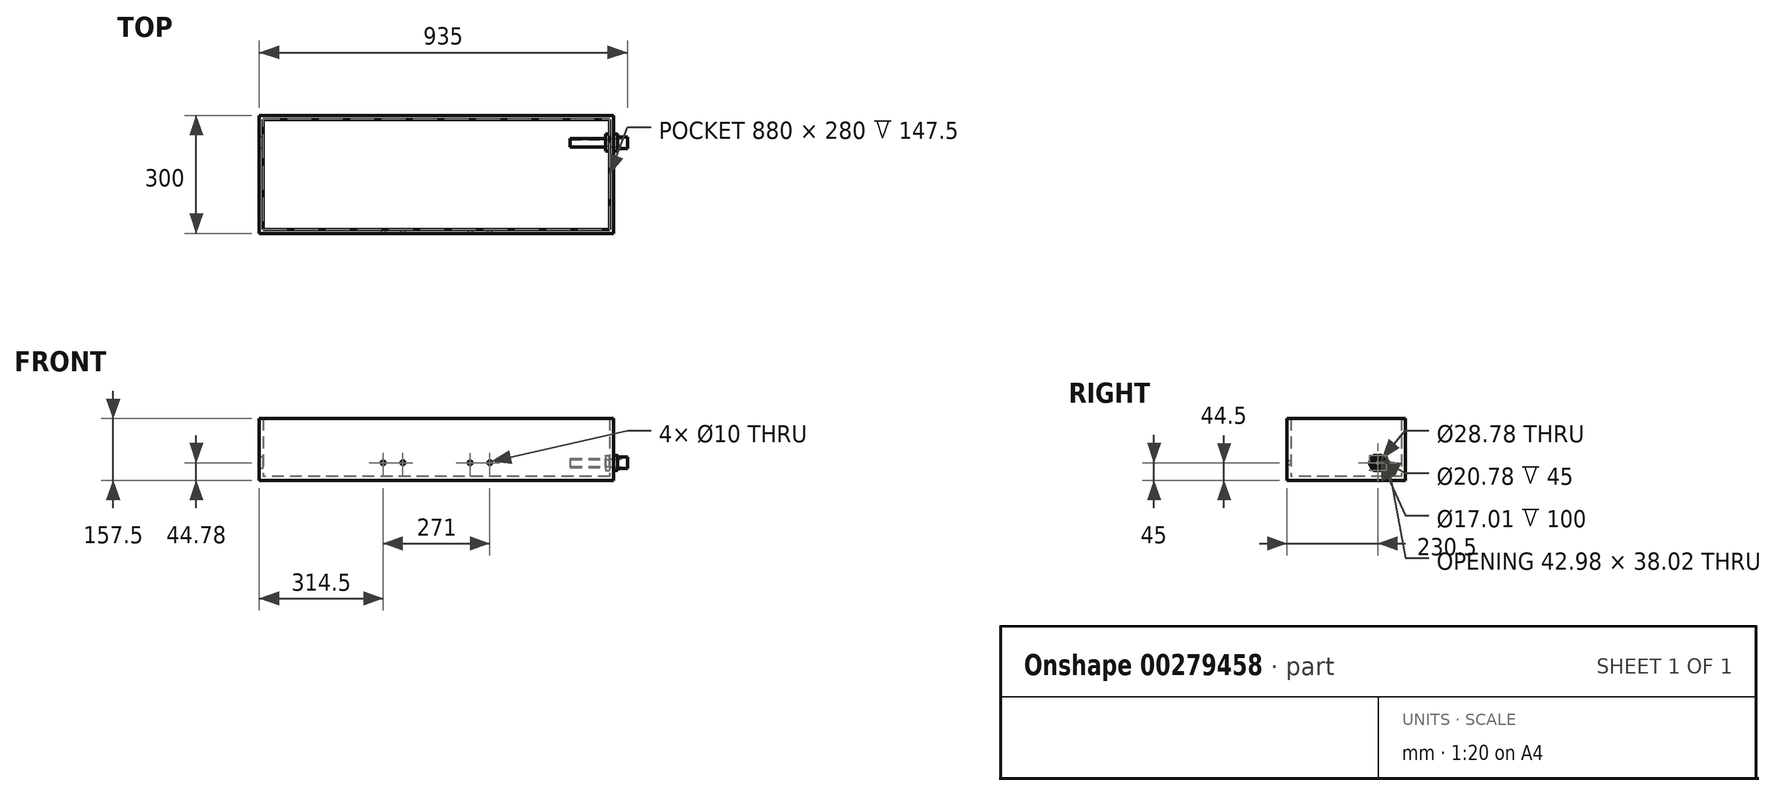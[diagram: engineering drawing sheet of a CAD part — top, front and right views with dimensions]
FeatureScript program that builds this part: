
annotation { "Feature Type Name" : "Feature", "Feature Type Description" : "" }
export const myFeature = defineFeature(function(context is Context, id is Id, definition is map)
    precondition{}
    {
        {
            var Q0;
            Q0=qCreatedBy(makeId("Top.planeOp"),FACE);
            var sketch = newSketch(context, id + "F0", { "sketchPlane" : qUnion([Q0])});
            skLineSegment(sketch, "E0.bottom", {"start": v(450, 150) * mm, "end": v(-450, 150) * mm});
            skLineSegment(sketch, "E0.top", {"start": v(450, -150) * mm, "end": v(-450, -150) * mm});
            skLineSegment(sketch, "E0.left", {"start": v(450, 150) * mm, "end": v(450, -150) * mm});
            skLineSegment(sketch, "E0.right", {"start": v(-450, 150) * mm, "end": v(-450, -150) * mm});
            skPoint(sketch, "E0.middle", {"position": v(0, 0) * mm});
            skSolve(sketch);
        }
        {
            var Q0;
            Q0=qSketchRegion(id+"F0",true);
            extrude(context, id + "F1", {"entities" : qUnion([Q0]), "depth" : 7.5 * mm});
        }
        {
            var Q0;
            Q0=makeQuery(id+"F1.opExtrude","CAP_FACE",FACE,{"disambiguationData":[OSD([sQuery(id+"F0.wireOp",EDGE,"E0.bottom"),sQuery(id+"F0.wireOp",EDGE,"E0.top"),sQuery(id+"F0.wireOp",EDGE,"E0.left"),sQuery(id+"F0.wireOp",EDGE,"E0.right")])],"isStart":false});
            var sketch = newSketch(context, id + "F2", { "sketchPlane" : qUnion([Q0])});
            skLineSegment(sketch, "E1.bottom", {"start": v(442.5, 142.5) * mm, "end": v(-442.5, 142.5) * mm});
            skLineSegment(sketch, "E1.top", {"start": v(442.5, -142.5) * mm, "end": v(-442.5, -142.5) * mm});
            skLineSegment(sketch, "E1.left", {"start": v(442.5, 142.5) * mm, "end": v(442.5, -142.5) * mm});
            skLineSegment(sketch, "E1.right", {"start": v(-442.5, 142.5) * mm, "end": v(-442.5, -142.5) * mm});
            skPoint(sketch, "E1.middle", {"position": v(0, 0) * mm});
            skLineSegment(sketch, "E2.bottom", {"start": v(450, 150) * mm, "end": v(-450, 150) * mm});
            skLineSegment(sketch, "E2.top", {"start": v(450, -150) * mm, "end": v(-450, -150) * mm});
            skLineSegment(sketch, "E2.left", {"start": v(450, 150) * mm, "end": v(450, -150) * mm});
            skLineSegment(sketch, "E2.right", {"start": v(-450, 150) * mm, "end": v(-450, -150) * mm});
            skSolve(sketch);
        }
        {
            var Q0;
            Q0=qSketchRegion(id+"F2",true);
            extrude(context, id + "F3", {"entities" : qUnion([Q0]), "operationType" : NewBodyOperationType.ADD, "depth" : 150 * mm});
        }
        {
            var Q0;
            Q0=makeQuery(id+"F1.opExtrude","CAP_FACE",FACE,{"disambiguationData":[OSD([sQuery(id+"F0.wireOp",EDGE,"E0.bottom"),sQuery(id+"F0.wireOp",EDGE,"E0.top"),sQuery(id+"F0.wireOp",EDGE,"E0.left"),sQuery(id+"F0.wireOp",EDGE,"E0.right")])],"isStart":false});
            extrude(context, id + "F4", {"entities" : qUnion([Q0]), "depth" : 2.5 * mm});
        }
        {
            var Q0;
            Q0=makeQuery(id+"F4.opExtrude","CAP_FACE",FACE,{"disambiguationData":[OSD([sQuery(id+"F0.wireOp",EDGE,"E0.bottom"),sQuery(id+"F0.wireOp",EDGE,"E0.top"),sQuery(id+"F0.wireOp",EDGE,"E0.left"),sQuery(id+"F0.wireOp",EDGE,"E0.right")])],"isStart":false});
            var sketch = newSketch(context, id + "F5", { "sketchPlane" : qUnion([Q0])});
            skLineSegment(sketch, "E3.bottom", {"start": v(442.5, 142.5) * mm, "end": v(-442.5, 142.5) * mm});
            skLineSegment(sketch, "E3.top", {"start": v(442.5, -142.5) * mm, "end": v(-442.5, -142.5) * mm});
            skLineSegment(sketch, "E3.left", {"start": v(442.5, 142.5) * mm, "end": v(442.5, -142.5) * mm});
            skLineSegment(sketch, "E3.right", {"start": v(-442.5, 142.5) * mm, "end": v(-442.5, -142.5) * mm});
            skPoint(sketch, "E3.middle", {"position": v(0, 0) * mm});
            skLineSegment(sketch, "E4.bottom", {"start": v(440, 140) * mm, "end": v(-440, 140) * mm});
            skLineSegment(sketch, "E4.top", {"start": v(440, -140) * mm, "end": v(-440, -140) * mm});
            skLineSegment(sketch, "E4.left", {"start": v(440, 140) * mm, "end": v(440, -140) * mm});
            skLineSegment(sketch, "E4.right", {"start": v(-440, 140) * mm, "end": v(-440, -140) * mm});
            skSolve(sketch);
        }
        {
            var Q0;
            Q0=qSketchRegion(id+"F5",true);
            extrude(context, id + "F6", {"entities" : qUnion([Q0]), "operationType" : NewBodyOperationType.ADD, "depth" : 147.5 * mm});
        }
        {
            var Q0;
            Q0=makeQuery(id+"F3.boolean.opBoolean","MERGE",FACE,{"derivedFrom":[makeQuery(id+"F1.opExtrude","SWEPT_FACE",FACE,{"disambiguationData":[OSD([sQuery(id+"F0.wireOp",EDGE,"E0.top")])]}),makeQuery(id+"F3.opExtrude","SWEPT_FACE",FACE,{"disambiguationData":[OSD([sQuery(id+"F2.wireOp",EDGE,"E2.top")])]})]});
            var sketch = newSketch(context, id + "F7", { "sketchPlane" : qUnion([Q0])});
            skLineSegment(sketch, "E5.bottom", {"start": v(354.25, 147.22) * mm, "end": v(-354.25, 147.22) * mm, "construction": true});
            skLineSegment(sketch, "E5.top", {"start": v(354.25, 15) * mm, "end": v(-354.25, 15) * mm, "construction": true});
            skLineSegment(sketch, "E5.left", {"start": v(354.25, 147.22) * mm, "end": v(354.25, 15) * mm, "construction": true});
            skLineSegment(sketch, "E5.right", {"start": v(-354.25, 147.22) * mm, "end": v(-354.25, 15) * mm, "construction": true});
            skPoint(sketch, "E5.middle", {"position": v(0, 78.75) * mm});
            skPoint(sketch, "E5.middle.positionSnap0", {"position": v(-450, 78.75) * mm});
            skPoint(sketch, "E5.centerSnap0", {"position": v(-450, 78.75) * mm});
            skCircle(sketch, "E6", {"center": v(85.5, 44.78) * mm, "radius": 5 * mm});
            skLineSegment(sketch, "E7", {"start": v(85.5, 44.78) * mm, "end": v(85.5, 15) * mm, "construction": true});
            skLineSegment(sketch, "E8", {"start": v(85.5, 44.78) * mm, "end": v(354.25, 44.78) * mm, "construction": true});
            skCircle(sketch, "E9.1.0.0", {"center": v(135.5, 44.78) * mm, "radius": 5 * mm});
            skLineSegment(sketch, "E9.direction1", {"start": v(85.5, 44.78) * mm, "end": v(135.5, 44.78) * mm, "construction": true});
            skCircle(sketch, "E10", {"center": v(-85.5, 44.78) * mm, "radius": 5 * mm});
            skLineSegment(sketch, "E11", {"start": v(-85.5, 15) * mm, "end": v(-85.5, 44.78) * mm, "construction": true});
            skLineSegment(sketch, "E12", {"start": v(-85.5, 44.78) * mm, "end": v(-354.25, 44.78) * mm, "construction": true});
            skCircle(sketch, "E13.1.0.0", {"center": v(-135.5, 44.78) * mm, "radius": 5 * mm});
            skLineSegment(sketch, "E13.direction1", {"start": v(-85.5, 44.78) * mm, "end": v(-135.5, 44.78) * mm, "construction": true});
            skSolve(sketch);
        }
        {
            var Q0;
            Q0=qSketchRegion(id+"F7",true);
            extrude(context, id + "F8", {"entities" : qUnion([Q0]), "operationType" : NewBodyOperationType.REMOVE, "oppositeDirection" : true, "depth" : 25 * mm});
        }
        {
            var Q0;
            Q0=makeQuery(id+"F3.boolean.opBoolean","MERGE",FACE,{"derivedFrom":[makeQuery(id+"F1.opExtrude","SWEPT_FACE",FACE,{"disambiguationData":[OSD([sQuery(id+"F0.wireOp",EDGE,"E0.right")])]}),makeQuery(id+"F3.opExtrude","SWEPT_FACE",FACE,{"disambiguationData":[OSD([sQuery(id+"F2.wireOp",EDGE,"E2.right")])]})]});
            var sketch = newSketch(context, id + "F9", { "sketchPlane" : qUnion([Q0])});
            skCircle(sketch, "E14", {"center": v(-80.5, 45) * mm, "radius": 14.4 * mm});
            skLineSegment(sketch, "E15", {"start": v(-80.5, 45) * mm, "end": v(-80.5, 0) * mm, "construction": true});
            skLineSegment(sketch, "E16", {"start": v(-80.5, 45) * mm, "end": v(-150, 45) * mm, "construction": true});
            skSolve(sketch);
        }
        {
            var Q0;
            Q0=qSketchRegion(id+"F9",true);
            extrude(context, id + "F10", {"entities" : qUnion([Q0]), "operationType" : NewBodyOperationType.REMOVE, "oppositeDirection" : true, "depth" : 500 * mm});
        }
        {
            var Q0;
            Q0=makeQuery(id+"F3.boolean.opBoolean","MERGE",FACE,{"derivedFrom":[makeQuery(id+"F1.opExtrude","SWEPT_FACE",FACE,{"disambiguationData":[OSD([sQuery(id+"F0.wireOp",EDGE,"E0.left")])]}),makeQuery(id+"F3.opExtrude","SWEPT_FACE",FACE,{"disambiguationData":[OSD([sQuery(id+"F2.wireOp",EDGE,"E2.left")])]})]});
            var sketch = newSketch(context, id + "F11", { "sketchPlane" : qUnion([Q0])});
            skCircle(sketch, "E17", {"center": v(80.5, 44.5) * mm, "radius": 14.4 * mm});
            skLineSegment(sketch, "E18", {"start": v(80.5, 0) * mm, "end": v(80.5, 44.5) * mm, "construction": true});
            skLineSegment(sketch, "E19", {"start": v(150, 44.5) * mm, "end": v(80.5, 44.5) * mm, "construction": true});
            skSolve(sketch);
        }
        {
            var Q0;
            Q0=qSketchRegion(id+"F11",true);
            extrude(context, id + "F12", {"entities" : qUnion([Q0]), "operationType" : NewBodyOperationType.REMOVE, "oppositeDirection" : true, "depth" : 25 * mm});
        }
        {
            var Q0;
            Q0=makeQuery(id+"F3.boolean.opBoolean","MERGE",FACE,{"derivedFrom":[makeQuery(id+"F1.opExtrude","SWEPT_FACE",FACE,{"disambiguationData":[OSD([sQuery(id+"F0.wireOp",EDGE,"E0.left")])]}),makeQuery(id+"F3.opExtrude","SWEPT_FACE",FACE,{"disambiguationData":[OSD([sQuery(id+"F2.wireOp",EDGE,"E2.left")])]})]});
            var sketch = newSketch(context, id + "F13", { "sketchPlane" : qUnion([Q0])});
            skCircle(sketch, "E20", {"center": v(80.5, 44.5) * mm, "radius": 10.4 * mm});
            skCircle(sketch, "E21", {"center": v(80.5, 44.5) * mm, "radius": 14.4 * mm});
            skSolve(sketch);
        }
        {
            var Q0;
            Q0=qSketchRegion(id+"F13",true);
            extrude(context, id + "F14", {"entities" : qUnion([Q0]), "oppositeDirection" : true, "depth" : 10 * mm});
        }
        {
            var Q0;
            Q0=makeQuery(id+"F14.opExtrude","CAP_FACE",FACE,{"disambiguationData":[OSD([sQuery(id+"F13.wireOp",EDGE,"E20"),sQuery(id+"F13.wireOp",EDGE,"E21")])],"isStart":true});
            var sketch = newSketch(context, id + "F15", { "sketchPlane" : qUnion([Q0])});
            skCircle(sketch, "E22.cCircle", {"center": v(80.5, 44.5) * mm, "radius": 19.01 * mm, "construction": true});
            skLineSegment(sketch, "E22.0", {"start": v(71.26, 63.51) * mm, "end": v(89.74, 63.51) * mm});
            skLineSegment(sketch, "E22.1", {"start": v(92.34, 62.01) * mm, "end": v(101.59, 46) * mm});
            skLineSegment(sketch, "E22.2", {"start": v(101.59, 43) * mm, "end": v(92.34, 26.99) * mm});
            skLineSegment(sketch, "E22.3", {"start": v(89.74, 25.49) * mm, "end": v(71.26, 25.49) * mm});
            skLineSegment(sketch, "E22.4", {"start": v(68.66, 26.99) * mm, "end": v(59.41, 43) * mm});
            skLineSegment(sketch, "E22.5", {"start": v(59.41, 46) * mm, "end": v(68.66, 62.01) * mm});
            skPoint(sketch, "E22.0.midPoint", {"position": v(80.5, 63.51) * mm});
            skCircle(sketch, "E23", {"center": v(80.5, 44.5) * mm, "radius": 10.4 * mm});
            skPoint(sketch, "E24.visualSharp", {"position": v(69.52, 63.51) * mm});
            skArc(sketch, "E24.filletArc", {"start": v(71.26, 63.51) * mm, "mid": v(69.76, 63.11) * mm, "end": v(68.66, 62.01) * mm});
            skPoint(sketch, "E25.visualSharp", {"position": v(91.48, 63.51) * mm});
            skArc(sketch, "E25.filletArc", {"start": v(92.34, 62.01) * mm, "mid": v(91.24, 63.11) * mm, "end": v(89.74, 63.51) * mm});
            skPoint(sketch, "E26.visualSharp", {"position": v(102.45, 44.5) * mm});
            skArc(sketch, "E26.filletArc", {"start": v(101.59, 43) * mm, "mid": v(101.99, 44.5) * mm, "end": v(101.59, 46) * mm});
            skPoint(sketch, "E27.visualSharp", {"position": v(91.48, 25.49) * mm});
            skArc(sketch, "E27.filletArc", {"start": v(89.74, 25.49) * mm, "mid": v(91.24, 25.89) * mm, "end": v(92.34, 26.99) * mm});
            skPoint(sketch, "E28.visualSharp", {"position": v(69.52, 25.49) * mm});
            skArc(sketch, "E28.filletArc", {"start": v(68.66, 26.99) * mm, "mid": v(69.76, 25.89) * mm, "end": v(71.26, 25.49) * mm});
            skPoint(sketch, "E29.visualSharp", {"position": v(58.55, 44.5) * mm});
            skArc(sketch, "E29.filletArc", {"start": v(59.41, 46) * mm, "mid": v(59.01, 44.5) * mm, "end": v(59.41, 43) * mm});
            skSolve(sketch);
        }
        {
            var Q0;
            Q0=qSketchRegion(id+"F15",true);
            extrude(context, id + "F16", {"entities" : qUnion([Q0]), "operationType" : NewBodyOperationType.ADD, "depth" : 10 * mm});
        }
        {
            var Q0;
            Q0=makeQuery(id+"F16.opExtrude","CAP_FACE",FACE,{"disambiguationData":[OSD([sQuery(id+"F15.wireOp",EDGE,"E22.0"),sQuery(id+"F15.wireOp",EDGE,"E22.1"),sQuery(id+"F15.wireOp",EDGE,"E22.2"),sQuery(id+"F15.wireOp",EDGE,"E22.3"),sQuery(id+"F15.wireOp",EDGE,"E22.4"),sQuery(id+"F15.wireOp",EDGE,"E22.5"),sQuery(id+"F15.wireOp",EDGE,"E23"),sQuery(id+"F15.wireOp",EDGE,"E24.filletArc"),sQuery(id+"F15.wireOp",EDGE,"E25.filletArc"),sQuery(id+"F15.wireOp",EDGE,"E26.filletArc"),sQuery(id+"F15.wireOp",EDGE,"E27.filletArc"),sQuery(id+"F15.wireOp",EDGE,"E28.filletArc"),sQuery(id+"F15.wireOp",EDGE,"E29.filletArc")])],"isStart":false});
            var sketch = newSketch(context, id + "F17", { "sketchPlane" : qUnion([Q0])});
            skCircle(sketch, "E30", {"center": v(80.5, 44.5) * mm, "radius": 14.62 * mm});
            skCircle(sketch, "E31", {"center": v(80.5, 44.5) * mm, "radius": 10.4 * mm});
            skSolve(sketch);
        }
        {
            var Q0;
            Q0=qSketchRegion(id+"F17",true);
            extrude(context, id + "F18", {"entities" : qUnion([Q0]), "operationType" : NewBodyOperationType.ADD, "depth" : 25 * mm});
        }
        {
            var Q0;
            Q0=makeQuery(id+"F14.opExtrude","CAP_FACE",FACE,{"disambiguationData":[OSD([sQuery(id+"F13.wireOp",EDGE,"E20"),sQuery(id+"F13.wireOp",EDGE,"E21")])],"isStart":false});
            var sketch = newSketch(context, id + "F19", { "sketchPlane" : qUnion([Q0])});
            skCircle(sketch, "E32", {"center": v(-80.5, 44.5) * mm, "radius": 8.5 * mm});
            skCircle(sketch, "E33", {"center": v(-80.5, 44.5) * mm, "radius": 11.24 * mm});
            skSolve(sketch);
        }
        {
            var Q0;
            Q0=qSketchRegion(id+"F19",true);
            extrude(context, id + "F20", {"entities" : qUnion([Q0]), "operationType" : NewBodyOperationType.ADD, "depth" : 50 * mm});
        }
        {
            var Q0;
            Q0=makeQuery(id+"F14.opExtrude","CAP_FACE",FACE,{"disambiguationData":[OSD([sQuery(id+"F13.wireOp",EDGE,"E20"),sQuery(id+"F13.wireOp",EDGE,"E21")])],"isStart":false});
            var sketch = newSketch(context, id + "F21", { "sketchPlane" : qUnion([Q0])});
            skCircle(sketch, "E34.cCircle", {"center": v(-80.5, 44.5) * mm, "radius": 19.01 * mm, "construction": true});
            skLineSegment(sketch, "E34.0", {"start": v(-89.74, 63.51) * mm, "end": v(-71.26, 63.51) * mm});
            skLineSegment(sketch, "E34.1", {"start": v(-68.66, 62.01) * mm, "end": v(-59.41, 46) * mm});
            skLineSegment(sketch, "E34.2", {"start": v(-59.41, 43) * mm, "end": v(-68.66, 26.99) * mm});
            skLineSegment(sketch, "E34.3", {"start": v(-71.26, 25.49) * mm, "end": v(-89.74, 25.49) * mm});
            skLineSegment(sketch, "E34.4", {"start": v(-92.34, 26.99) * mm, "end": v(-101.59, 43) * mm});
            skLineSegment(sketch, "E34.5", {"start": v(-101.59, 46) * mm, "end": v(-92.34, 62.01) * mm});
            skPoint(sketch, "E34.0.midPoint", {"position": v(-80.5, 63.51) * mm});
            skPoint(sketch, "E35.visualSharp", {"position": v(-91.48, 63.51) * mm});
            skArc(sketch, "E35.filletArc", {"start": v(-89.74, 63.51) * mm, "mid": v(-91.24, 63.11) * mm, "end": v(-92.34, 62.01) * mm});
            skPoint(sketch, "E36.visualSharp", {"position": v(-69.52, 63.51) * mm});
            skArc(sketch, "E36.filletArc", {"start": v(-68.66, 62.01) * mm, "mid": v(-69.76, 63.11) * mm, "end": v(-71.26, 63.51) * mm});
            skPoint(sketch, "E37.visualSharp", {"position": v(-58.55, 44.5) * mm});
            skArc(sketch, "E37.filletArc", {"start": v(-59.41, 43) * mm, "mid": v(-59.01, 44.5) * mm, "end": v(-59.41, 46) * mm});
            skPoint(sketch, "E38.visualSharp", {"position": v(-69.52, 25.49) * mm});
            skArc(sketch, "E38.filletArc", {"start": v(-71.26, 25.49) * mm, "mid": v(-69.76, 25.89) * mm, "end": v(-68.66, 26.99) * mm});
            skPoint(sketch, "E39.visualSharp", {"position": v(-91.48, 25.49) * mm});
            skArc(sketch, "E39.filletArc", {"start": v(-92.34, 26.99) * mm, "mid": v(-91.24, 25.89) * mm, "end": v(-89.74, 25.49) * mm});
            skPoint(sketch, "E40.visualSharp", {"position": v(-102.45, 44.5) * mm});
            skArc(sketch, "E40.filletArc", {"start": v(-101.59, 46) * mm, "mid": v(-101.99, 44.5) * mm, "end": v(-101.59, 43) * mm});
            skCircle(sketch, "E41", {"center": v(-80.5, 44.5) * mm, "radius": 11.24 * mm});
            skSolve(sketch);
        }
        {
            var Q0;
            Q0=qSketchRegion(id+"F21",true);
            extrude(context, id + "F22", {"entities" : qUnion([Q0]), "operationType" : NewBodyOperationType.ADD, "depth" : 10 * mm});
        }
        {
            var Q0;
            Q0=makeQuery(id+"F20.opExtrude","CAP_FACE",FACE,{"disambiguationData":[OSD([sQuery(id+"F19.wireOp",EDGE,"E32"),sQuery(id+"F19.wireOp",EDGE,"E33")])],"isStart":false});
            extrude(context, id + "F23", {"entities" : qUnion([Q0]), "operationType" : NewBodyOperationType.ADD, "depth" : 50 * mm});
        }
    });
